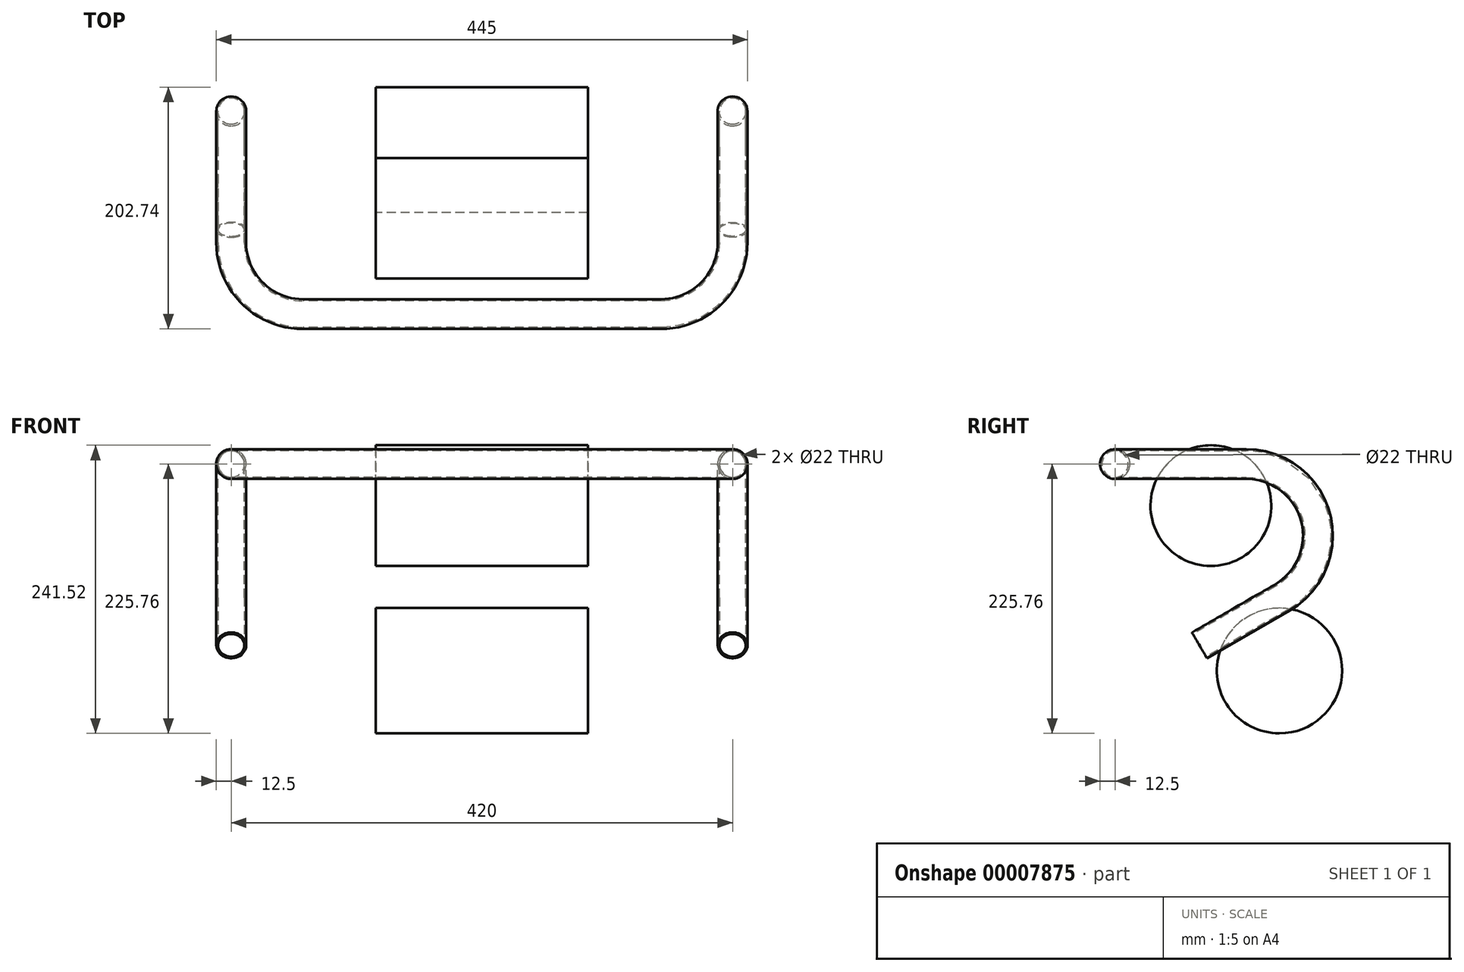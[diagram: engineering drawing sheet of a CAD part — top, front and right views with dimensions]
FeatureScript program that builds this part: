
annotation { "Feature Type Name" : "Feature", "Feature Type Description" : "" }
export const myFeature = defineFeature(function(context is Context, id is Id, definition is map)
    precondition{}
    {
        {
            var Q0;
            Q0=qCreatedBy(makeId("Right.planeOp"),FACE);
            var sketch = newSketch(context, id + "F0", { "sketchPlane" : qUnion([Q0])});
            skCircle(sketch, "E0", {"center": v(0, 0) * mm, "radius": 12.5 * mm});
            skCircle(sketch, "E1.0", {"center": v(0, 0) * mm, "radius": 11 * mm});
            skSolve(sketch);
        }
        {
            var Q0;
            Q0=qCreatedBy(makeId("Top.planeOp"),FACE);
            var sketch = newSketch(context, id + "F1", { "sketchPlane" : qUnion([Q0])});
            skLineSegment(sketch, "E2", {"start": v(-150, 0) * mm, "end": v(0, 0) * mm});
            skArc(sketch, "E3", {"start": v(150, 0) * mm, "mid": v(192.43, 17.57) * mm, "end": v(210, 60) * mm});
            skArc(sketch, "E4", {"start": v(-150, 0) * mm, "mid": v(-192.43, 17.57) * mm, "end": v(-210, 60) * mm});
            skLineSegment(sketch, "E5", {"start": v(210, 60) * mm, "end": v(210, 110) * mm});
            skLineSegment(sketch, "E6", {"start": v(-210, 60) * mm, "end": v(-210, 110) * mm});
            skLineSegment(sketch, "E7", {"start": v(150, 0) * mm, "end": v(150, 60) * mm, "construction": true});
            skLineSegment(sketch, "E8", {"start": v(210, 60) * mm, "end": v(150, 60) * mm, "construction": true});
            skLineSegment(sketch, "E9", {"start": v(-210, 60) * mm, "end": v(-150, 60) * mm, "construction": true});
            skLineSegment(sketch, "E10", {"start": v(-150, 60) * mm, "end": v(-150, 0) * mm, "construction": true});
            skLineSegment(sketch, "E11", {"start": v(0, 0) * mm, "end": v(150, 0) * mm});
            skSolve(sketch);
        }
        {
            var Q0;
            Q0=sQuery(id+"F1.wireOp",EDGE,"E5");
            cPlane(context, id + "F2", {"entities" : qUnion([Q0]), "cplaneType" : CPlaneType.LINE_ANGLE, "offset" : 150 * mm, "angle" : 90 * degree, "width" : 150 * mm, "height" : 150 * mm});
        }
        {
            var Q0;
            Q0=sQuery(id+"F1.wireOp",EDGE,"E6");
            cPlane(context, id + "F3", {"entities" : qUnion([Q0]), "cplaneType" : CPlaneType.LINE_ANGLE, "offset" : 150 * mm, "angle" : 90 * degree, "width" : 150 * mm, "height" : 150 * mm});
        }
        {
            var Q0;
            Q0=qCreatedBy(id+"F2.planeOp",FACE);
            var sketch = newSketch(context, id + "F4", { "sketchPlane" : qUnion([Q0])});
            skArc(sketch, "E12", {"start": v(140, -111.96) * mm, "mid": v(167.96, -44.47) * mm, "end": v(110, 0) * mm});
            skLineSegment(sketch, "E13", {"start": v(110, 0) * mm, "end": v(110, -60) * mm, "construction": true});
            skLineSegment(sketch, "E14", {"start": v(140, -111.96) * mm, "end": v(110, -60) * mm, "construction": true});
            skLineSegment(sketch, "E15", {"start": v(140, -111.96) * mm, "end": v(70.72, -151.96) * mm});
            skSolve(sketch);
        }
        {
            var Q0;
            Q0=qCreatedBy(id+"F3.planeOp",FACE);
            var sketch = newSketch(context, id + "F5", { "sketchPlane" : qUnion([Q0])});
            skArc(sketch, "E16", {"start": v(140, -111.96) * mm, "mid": v(167.96, -44.47) * mm, "end": v(110, 0) * mm});
            skLineSegment(sketch, "E17", {"start": v(110, 0) * mm, "end": v(110, -60) * mm, "construction": true});
            skLineSegment(sketch, "E18", {"start": v(140, -111.96) * mm, "end": v(110, -60) * mm, "construction": true});
            skLineSegment(sketch, "E19", {"start": v(140, -111.96) * mm, "end": v(70.72, -151.96) * mm});
            skSolve(sketch);
        }
        {
            var Q0;
            Q0=makeQuery(id+"F0.imprint","IMPRINT",FACE,{"disambiguationData":[TD([[makeQuery(id+"F0.imprint","IMPRINT",EDGE,{"derivedFrom":sQuery(id+"F0.wireOp",EDGE,"E0")}),1.0]])]});
            var Q1;
            Q1=sQuery(id+"F1.wireOp",EDGE,"E2");
            var Q2;
            Q2=sQuery(id+"F1.wireOp",EDGE,"E4");
            var Q3;
            Q3=sQuery(id+"F1.wireOp",EDGE,"E6");
            var Q4;
            Q4=sQuery(id+"F5.wireOp",EDGE,"E16");
            var Q5;
            Q5=sQuery(id+"F5.wireOp",EDGE,"E19");
            sweep(context, id + "F6", {"profiles" : qUnion([Q0]), "path" : qUnion([Q1, Q2, Q3, Q4, Q5])});
        }
        {
            var Q0;
            Q0=makeQuery(id+"F0.imprint","IMPRINT",FACE,{"disambiguationData":[TD([[makeQuery(id+"F0.imprint","IMPRINT",EDGE,{"derivedFrom":sQuery(id+"F0.wireOp",EDGE,"E0")}),1.0]])]});
            var Q1;
            Q1=sQuery(id+"F1.wireOp",EDGE,"E11");
            var Q2;
            Q2=sQuery(id+"F1.wireOp",EDGE,"E3");
            var Q3;
            Q3=sQuery(id+"F1.wireOp",EDGE,"E5");
            var Q4;
            Q4=sQuery(id+"F4.wireOp",EDGE,"E12");
            var Q5;
            Q5=sQuery(id+"F4.wireOp",EDGE,"E15");
            sweep(context, id + "F7", {"operationType" : NewBodyOperationType.ADD, "profiles" : qUnion([Q0]), "path" : qUnion([Q1, Q2, Q3, Q4, Q5])});
        }
        {
            var Q0;
            Q0=qCreatedBy(makeId("Right.planeOp"),FACE);
            var sketch = newSketch(context, id + "F8", { "sketchPlane" : qUnion([Q0])});
            skCircle(sketch, "E20", {"center": v(80.33, -34.84) * mm, "radius": 50.6 * mm});
            skCircle(sketch, "E21", {"center": v(137.74, -173.26) * mm, "radius": 52.5 * mm});
            skSolve(sketch);
        }
        {
            var Q0;
            Q0 = qSketchRegion(id + "F8", true);
            extrude(context, id + "F9", {"entities" : qUnion([Q0]), "endBound" : BoundingType.SYMMETRIC, "depth" : 177.8 * mm});
        }
    });
